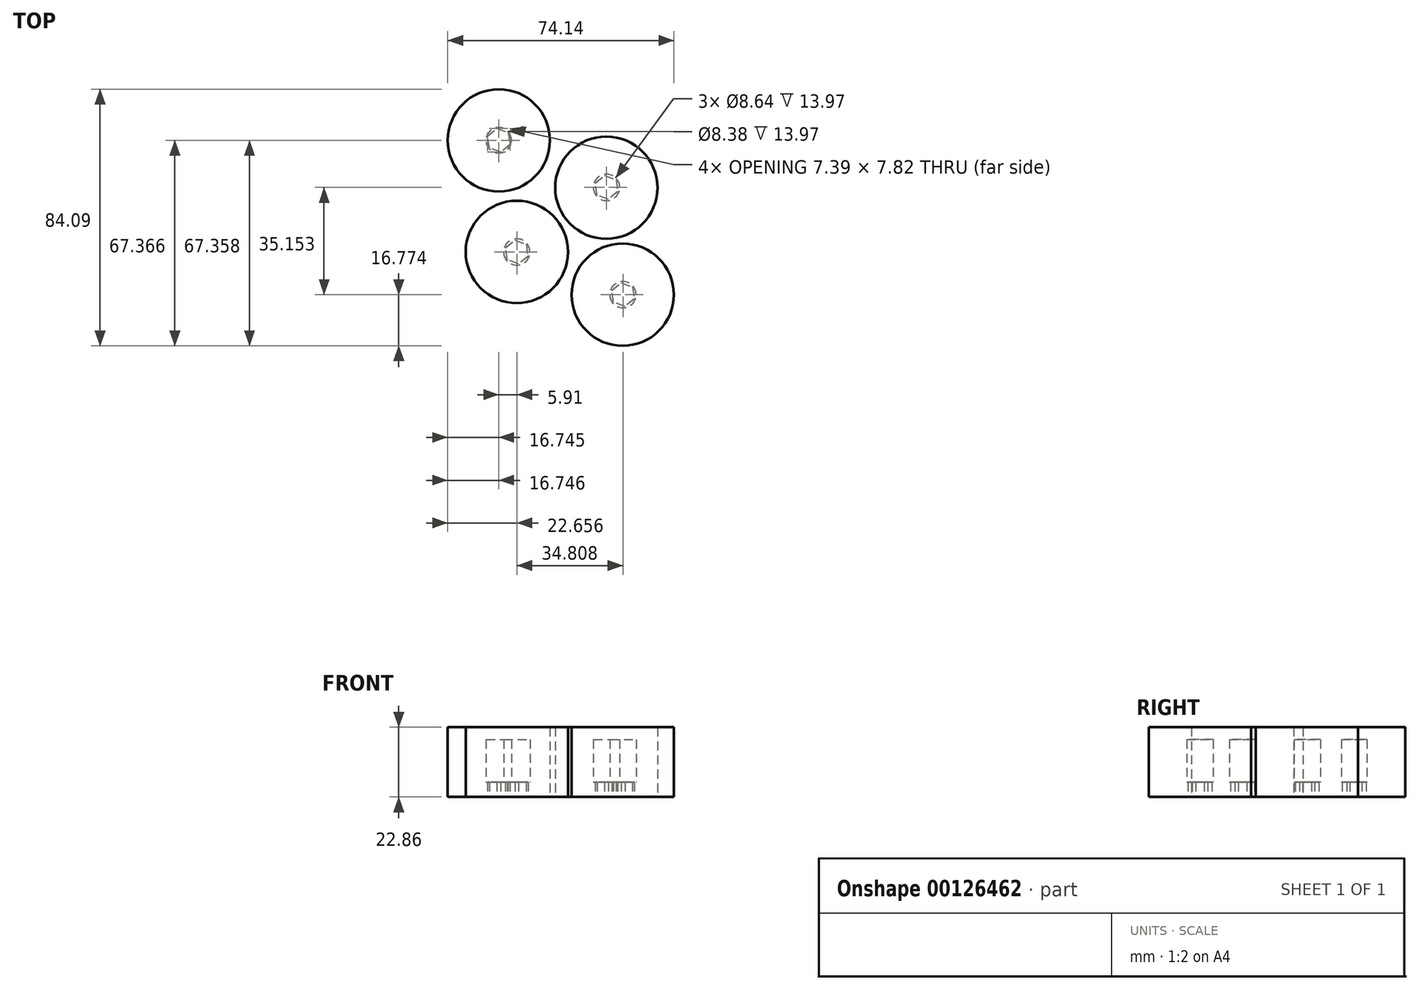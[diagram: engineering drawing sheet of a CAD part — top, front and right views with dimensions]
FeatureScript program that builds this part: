
annotation { "Feature Type Name" : "Feature", "Feature Type Description" : "" }
export const myFeature = defineFeature(function(context is Context, id is Id, definition is map)
    precondition{}
    {
        {
            var Q0;
            Q0=qCreatedBy(makeId("Top.planeOp"),FACE);
            var sketch = newSketch(context, id + "F0", { "sketchPlane" : qUnion([Q0])});
            skCircle(sketch, "E0", {"center": v(-27.13, 39.22) * mm, "radius": 16.76 * mm});
            skCircle(sketch, "E1", {"center": v(8.12, 23.72) * mm, "radius": 16.76 * mm});
            skCircle(sketch, "E2", {"center": v(-21.23, 2.68) * mm, "radius": 16.76 * mm});
            skCircle(sketch, "E3", {"center": v(13.47, -11.35) * mm, "radius": 16.76 * mm});
            skSolve(sketch);
        }
        {
            var Q0;
            Q0 = qSketchRegion(id + "F0", true);
            extrude(context, id + "F1", {"entities" : qUnion([Q0]), "depth" : 22.86 * mm});
        }
        {
            var Q0;
            Q0=qCreatedBy(makeId("Top.planeOp"),FACE);
            var sketch = newSketch(context, id + "F2", { "sketchPlane" : qUnion([Q0])});
            skCircle(sketch, "E4", {"center": v(-27.15, 39.26) * mm, "radius": 3.43 * mm, "construction": true});
            skLineSegment(sketch, "E5.0", {"start": v(-24.08, 41.75) * mm, "end": v(-23.46, 37.84) * mm});
            skLineSegment(sketch, "E5.1", {"start": v(-23.46, 37.84) * mm, "end": v(-26.53, 35.35) * mm});
            skLineSegment(sketch, "E5.2", {"start": v(-26.53, 35.35) * mm, "end": v(-30.23, 36.76) * mm});
            skLineSegment(sketch, "E5.3", {"start": v(-30.23, 36.76) * mm, "end": v(-30.85, 40.67) * mm});
            skLineSegment(sketch, "E5.4", {"start": v(-30.85, 40.67) * mm, "end": v(-27.78, 43.17) * mm});
            skLineSegment(sketch, "E5.5", {"start": v(-27.78, 43.17) * mm, "end": v(-24.08, 41.75) * mm});
            skPoint(sketch, "E5.0.midPoint", {"position": v(-23.77, 39.8) * mm});
            skCircle(sketch, "E6.cCircle", {"center": v(8.2, 23.82) * mm, "radius": 3.43 * mm, "construction": true});
            skLineSegment(sketch, "E6.0", {"start": v(11.27, 26.31) * mm, "end": v(11.9, 22.4) * mm});
            skLineSegment(sketch, "E6.1", {"start": v(11.9, 22.4) * mm, "end": v(8.82, 19.91) * mm});
            skLineSegment(sketch, "E6.2", {"start": v(8.82, 19.91) * mm, "end": v(5.12, 21.33) * mm});
            skLineSegment(sketch, "E6.3", {"start": v(5.12, 21.33) * mm, "end": v(4.5, 25.24) * mm});
            skLineSegment(sketch, "E6.4", {"start": v(4.5, 25.24) * mm, "end": v(7.58, 27.73) * mm});
            skLineSegment(sketch, "E6.5", {"start": v(7.58, 27.73) * mm, "end": v(11.27, 26.31) * mm});
            skCircle(sketch, "E7.cCircle", {"center": v(-21.24, 2.65) * mm, "radius": 3.43 * mm, "construction": true});
            skLineSegment(sketch, "E7.0", {"start": v(-18.17, 5.14) * mm, "end": v(-17.55, 1.23) * mm});
            skLineSegment(sketch, "E7.1", {"start": v(-17.55, 1.23) * mm, "end": v(-20.62, -1.26) * mm});
            skLineSegment(sketch, "E7.2", {"start": v(-20.62, -1.26) * mm, "end": v(-24.32, 0.16) * mm});
            skLineSegment(sketch, "E7.3", {"start": v(-24.32, 0.16) * mm, "end": v(-24.94, 4.07) * mm});
            skLineSegment(sketch, "E7.4", {"start": v(-24.94, 4.07) * mm, "end": v(-21.87, 6.56) * mm});
            skLineSegment(sketch, "E7.5", {"start": v(-21.87, 6.56) * mm, "end": v(-18.17, 5.14) * mm});
            skCircle(sketch, "E8.cCircle", {"center": v(13.58, -11.31) * mm, "radius": 3.43 * mm, "construction": true});
            skLineSegment(sketch, "E8.0", {"start": v(16.65, -8.82) * mm, "end": v(17.27, -12.73) * mm});
            skLineSegment(sketch, "E8.1", {"start": v(17.27, -12.73) * mm, "end": v(14.2, -15.22) * mm});
            skLineSegment(sketch, "E8.2", {"start": v(14.2, -15.22) * mm, "end": v(10.5, -13.8) * mm});
            skLineSegment(sketch, "E8.3", {"start": v(10.5, -13.8) * mm, "end": v(9.88, -9.9) * mm});
            skLineSegment(sketch, "E8.4", {"start": v(9.88, -9.9) * mm, "end": v(12.96, -7.4) * mm});
            skLineSegment(sketch, "E8.5", {"start": v(12.96, -7.4) * mm, "end": v(16.65, -8.82) * mm});
            skSolve(sketch);
        }
        {
            var Q0;
            Q0 = qSketchRegion(id + "F2", true);
            extrude(context, id + "F3", {"entities" : qUnion([Q0]), "operationType" : NewBodyOperationType.REMOVE, "depth" : 4.83 * mm});
        }
        {
            var Q0;
            Q0=makeQuery(id+"F3.boolean.opBoolean","COPY",FACE,{"derivedFrom":makeQuery(id+"F3.opExtrude","CAP_FACE",FACE,{"disambiguationData":[OSD([sQuery(id+"F2.wireOp",EDGE,"E7.0"),sQuery(id+"F2.wireOp",EDGE,"E7.1"),sQuery(id+"F2.wireOp",EDGE,"E7.2"),sQuery(id+"F2.wireOp",EDGE,"E7.3"),sQuery(id+"F2.wireOp",EDGE,"E7.4"),sQuery(id+"F2.wireOp",EDGE,"E7.5")])],"isStart":false})});
            var sketch = newSketch(context, id + "F4", { "sketchPlane" : qUnion([Q0])});
            skLineSegment(sketch, "E9", {"start": v(-24.32, -0.16) * mm, "end": v(-18.17, -5.14) * mm, "construction": true});
            skLineSegment(sketch, "E10", {"start": v(-18.17, -5.14) * mm, "end": v(-21.87, -6.56) * mm, "construction": true});
            skLineSegment(sketch, "E11", {"start": v(-21.87, -6.56) * mm, "end": v(-20.62, 1.26) * mm, "construction": true});
            skLineSegment(sketch, "E12", {"start": v(14.2, 15.23) * mm, "end": v(12.93, 7.4) * mm, "construction": true});
            skLineSegment(sketch, "E13", {"start": v(12.93, 7.4) * mm, "end": v(16.65, 8.83) * mm, "construction": true});
            skLineSegment(sketch, "E14", {"start": v(16.65, 8.83) * mm, "end": v(10.5, 13.82) * mm, "construction": true});
            skLineSegment(sketch, "E15", {"start": v(8.8, -19.93) * mm, "end": v(7.57, -27.74) * mm, "construction": true});
            skLineSegment(sketch, "E16", {"start": v(7.57, -27.74) * mm, "end": v(11.27, -26.29) * mm, "construction": true});
            skLineSegment(sketch, "E17", {"start": v(11.27, -26.29) * mm, "end": v(5.12, -21.36) * mm, "construction": true});
            skLineSegment(sketch, "E18", {"start": v(-26.55, -35.35) * mm, "end": v(-27.76, -43.14) * mm, "construction": true});
            skLineSegment(sketch, "E19", {"start": v(-27.76, -43.14) * mm, "end": v(-24.08, -41.75) * mm, "construction": true});
            skLineSegment(sketch, "E20", {"start": v(-24.08, -41.75) * mm, "end": v(-30.22, -36.78) * mm, "construction": true});
            skCircle(sketch, "E21", {"center": v(-21.24, -2.65) * mm, "radius": 4.32 * mm});
            skCircle(sketch, "E22", {"center": v(13.56, 11.34) * mm, "radius": 4.32 * mm});
            skCircle(sketch, "E23", {"center": v(8.19, -23.82) * mm, "radius": 4.32 * mm});
            skCircle(sketch, "E24", {"center": v(-27.15, -39.25) * mm, "radius": 4.19 * mm});
            skSolve(sketch);
        }
        {
            var Q0;
            Q0 = qSketchRegion(id + "F4", true);
            extrude(context, id + "F5", {"entities" : qUnion([Q0]), "operationType" : NewBodyOperationType.REMOVE, "oppositeDirection" : true, "depth" : 13.97 * mm});
        }
    });
